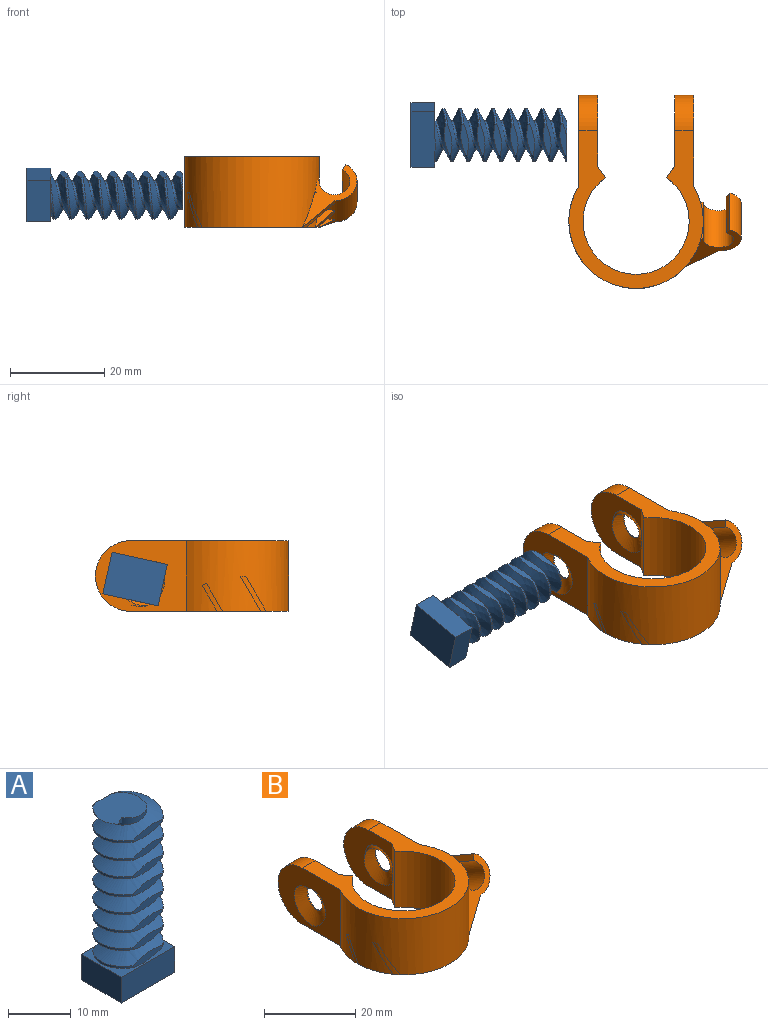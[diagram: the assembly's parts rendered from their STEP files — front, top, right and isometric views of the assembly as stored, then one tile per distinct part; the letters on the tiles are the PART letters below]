
ASSEMBLY  parts=2 mates=1
PART A: 45 faces, bbox 13.5x14.4x36.2 mm
  f0: bspline ~30.47x12.93mm, area 544.1mm2, adj f2,f3,f4,f5,f6,f7,f8,f9
  f1: bspline ~4.85x4.1mm, area 0.1mm2, adj f20,f22,f29
  f2: cylinder r=5.6mm len=9mm, axis (0,0,1), area 4.2mm2, adj f0,f18,f29,f37
  f3: cylinder r=5.6mm len=9mm, axis (0,0,1), area 4.2mm2, adj f0,f18,f30,f38
  f4: cylinder r=5.6mm len=9mm, axis (0,0,1), area 4.2mm2, adj f0,f18,f31,f39
  f5: cylinder r=5.6mm len=9mm, axis (0,0,1), area 4.2mm2, adj f0,f18,f32,f40
  f6: cylinder r=5.6mm len=9mm, axis (0,0,1), area 4.2mm2, adj f0,f18,f33,f41
  f7: cylinder r=5.6mm len=9mm, axis (0,0,1), area 4.2mm2, adj f0,f18,f34,f42
  f8: cylinder r=5.6mm len=9mm, axis (0,0,1), area 4.2mm2, adj f0,f18,f35,f43
  f9: cylinder r=5.6mm len=9mm, axis (0,0,1), area 4.2mm2, adj f0,f18,f36,f44
  f10: cylinder r=5.6mm len=8.51mm, axis (0,0,1), area 3.1mm2, adj f0,f18,f23,f44
  f11: cylinder r=5.6mm len=9mm, axis (0,0,1), area 4.2mm2, adj f0,f18,f36,f43
  f12: cylinder r=5.6mm len=9mm, axis (0,0,1), area 4.2mm2, adj f0,f18,f35,f42
  f13: cylinder r=5.6mm len=9mm, axis (0,0,1), area 4.2mm2, adj f0,f18,f34,f41
  f14: cylinder r=5.6mm len=9mm, axis (0,0,1), area 4.2mm2, adj f0,f18,f33,f40
  f15: cylinder r=5.6mm len=9mm, axis (0,0,1), area 4.2mm2, adj f0,f18,f32,f39
  f16: cylinder r=5.6mm len=9mm, axis (0,0,1), area 4.2mm2, adj f0,f18,f31,f38
  f17: cylinder r=5.6mm len=9mm, axis (0,0,1), area 4.2mm2, adj f0,f18,f30,f37
  f18: bspline ~30.47x12.93mm, area 534.8mm2, adj f2,f3,f4,f5,f6,f7,f8,f9
  f19: plane 1.81x1mm, normal (0.43,-0.9,0), area 1mm2, adj f18,f21,f22
  f20: cylinder r=5.6mm len=3.96mm, axis (0,0,1), area 1.1mm2, adj f1,f18,f22,f29
  f21: cylinder r=3mm len=28mm, axis (0,0,-1), area 44.6mm2, adj f0,f18,f19,f22,f23
  f22: plane 9.26x8.01mm, normal (0,0,1), area 52.2mm2, adj f0,f1,f18,f19,f20,f21,f29
  f23: plane 13.5x10.5mm, normal (0,0,1), area 49.2mm2, adj f0,f10,f18,f21,f24,f25,f26,f27
  f24: plane 9x5mm, normal (1,0,0), area 45mm2, adj f23,f25,f27,f28
  f25: plane 12.82x6.02mm, normal (0,1,0), area 60.5mm2, adj f0,f23,f24,f26,f28
  f26: plane 9x5mm, normal (-1,0,0), area 45mm2, adj f23,f25,f27,f28
  f27: plane 12x5mm, normal (0,-1,0), area 60mm2, adj f23,f24,f26,f28
  f28: plane 12x9mm, normal (0,0,-1), area 108mm2, adj f24,f25,f26,f27
  f29: plane 7.04x1.82mm, normal (0,1,0), area 7mm2, adj f0,f1,f2,f18,f20,f22
  f30: plane 6.67x1.65mm, normal (0,1,0), area 7.4mm2, adj f0,f3,f17,f18
  f31: plane 6.67x1.65mm, normal (0,1,0), area 7.4mm2, adj f0,f4,f16,f18
  f32: plane 6.67x1.65mm, normal (0,1,0), area 7.4mm2, adj f0,f5,f15,f18
  f33: plane 6.67x1.65mm, normal (0,1,0), area 7.4mm2, adj f0,f6,f14,f18
  f34: plane 6.67x1.65mm, normal (0,1,0), area 7.4mm2, adj f0,f7,f13,f18
  f35: plane 6.67x1.65mm, normal (0,1,0), area 7.4mm2, adj f0,f8,f12,f18
  f36: plane 6.67x1.65mm, normal (0,1,0), area 7.4mm2, adj f0,f9,f11,f18
  f37: plane 6.67x1.65mm, normal (0,-1,0), area 7.4mm2, adj f0,f2,f17,f18
  f38: plane 6.67x1.65mm, normal (0,-1,0), area 7.4mm2, adj f0,f3,f16,f18
  f39: plane 6.67x1.65mm, normal (0,-1,0), area 7.4mm2, adj f0,f4,f15,f18
  f40: plane 6.67x1.65mm, normal (0,-1,0), area 7.4mm2, adj f0,f5,f14,f18
  f41: plane 6.67x1.65mm, normal (0,-1,0), area 7.4mm2, adj f0,f6,f13,f18
  f42: plane 6.67x1.65mm, normal (0,-1,0), area 7.4mm2, adj f0,f7,f12,f18
  f43: plane 6.67x1.65mm, normal (0,-1,0), area 7.4mm2, adj f0,f8,f11,f18
  f44: plane 6.67x1.65mm, normal (0,-1,0), area 7.4mm2, adj f0,f9,f10,f18
PART B: 37 faces, bbox 38.5x42.8x16.9 mm
  f0: cylinder r=3.15mm len=6.3mm, axis (-1,0,0), area 4.5mm2, adj f13,f14,f31,f32
  f1: cylinder r=3.15mm len=6.3mm, axis (-1,0,0), area 4.5mm2, adj f8,f9,f33,f34
  f2: cylinder r=4.75mm len=0.48mm, axis (0,-0.87,0.5), area 0.1mm2, adj f3,f22,f23
  f3: cylinder r=14.25mm len=28.5mm, axis (0,0,1), area 804.6mm2, adj f2,f4,f6,f8,f14,f15,f16,f20
  f4: cylinder r=14.25mm len=7.5mm, axis (0,0,1), area 10.2mm2, adj f3,f15
  f5: cylinder r=14.25mm len=5.07mm, axis (0,0,1), area 12.3mm2, adj f15,f19,f27,f30
  f6: cylinder r=14.25mm len=6mm, axis (0,0,1), area 6.7mm2, adj f3,f15
  f7: cylinder r=14.25mm len=6.94mm, axis (0,0,1), area 22.4mm2, adj f15,f19,f25,f28
  f8: plane 19.27x15mm, normal (1,0,0), area 192.2mm2, adj f1,f3,f15,f16,f33,f34,f36
  f9: plane 16.91x16.91mm, normal (-1,0,0), area 131.3mm2, adj f1,f10,f15,f16,f33,f34,f36
  f10: plane 15.88x3.33mm, normal (-0.82,0.57,0), area 42.1mm2, adj f9,f11,f15,f16,f33,f34
  f11: cylinder r=11.25mm len=22.5mm, axis (0,0,1), area 854.1mm2, adj f10,f12,f15,f16
  f12: plane 15x2.46mm, normal (0.82,0.57,0), area 45mm2, adj f11,f13,f15,f16
  f13: plane 15x15mm, normal (1,0,0), area 128.1mm2, adj f0,f12,f15,f16,f31,f32,f35
  f14: plane 19.27x15mm, normal (-1,0,0), area 192.1mm2, adj f0,f3,f15,f16,f31,f32,f35
  f15: plane 33.42x28.5mm, normal (0,0,-1), area 268.3mm2, adj f3,f4,f5,f6,f7,f8,f9,f10
  f16: plane 33.42x28.5mm, normal (0,0,1), area 268.3mm2, adj f3,f8,f9,f10,f11,f12,f13,f14
  f17: cylinder r=3.25mm len=10.83mm, axis (0,-0.87,0.5), area 125.1mm2, adj f18,f20,f21,f22
  f18: plane 8.44x5.63mm, normal (-0.87,0.25,0.43), area 13.5mm2, adj f17,f19,f21,f22
  f19: cylinder r=4.75mm len=12.23mm, axis (0,-0.87,0.5), area 135.4mm2, adj f5,f7,f18,f21,f22,f24,f25,f26
  f20: plane 7.94x4.66mm, normal (0.09,0.5,0.86), area 1.7mm2, adj f3,f17,f21,f22
  f21: plane 8.87x8.65mm, normal (0,0.87,-0.5), area 26.5mm2, adj f3,f17,f18,f19,f20,f29
  f22: plane 13.33x11.67mm, normal (0,-0.87,0.5), area 42.1mm2, adj f2,f3,f17,f18,f19,f20,f23,f24
  f23: bspline ~4.23x1.06mm, area 0.1mm2, adj f2,f3,f22
  f24: bspline ~6.9x5.64mm, area 9mm2, adj f15,f19,f22,f25
  f25: plane 7.22x6.25mm, normal (0,0.87,-0.5), area 15.2mm2, adj f7,f19,f24
  f26: bspline ~4.12x3.63mm, area 5.6mm2, adj f15,f19,f27,f28
  f27: plane 4.33x3.78mm, normal (0,0.87,-0.5), area 7.5mm2, adj f5,f19,f26
  f28: plane 4.94x4.18mm, normal (0,-0.87,0.5), area 8.9mm2, adj f7,f19,f26
  f29: bspline ~3.28x1.81mm, area 3.8mm2, adj f15,f19,f21,f30
  f30: plane 3.32x2.8mm, normal (0,-0.87,0.5), area 4.4mm2, adj f5,f19,f29
  f31: bspline ~14.9x12.9mm, area 127.9mm2, adj f0,f13,f14,f32
  f32: bspline ~14.9x12.9mm, area 127.9mm2, adj f0,f13,f14,f31
  f33: bspline ~14.9x12.9mm, area 129.4mm2, adj f1,f8,f9,f10,f34
  f34: bspline ~14.9x12.9mm, area 128.6mm2, adj f1,f8,f9,f10,f33
  f35: cylinder r=7.5mm len=15mm, axis (1,0,0), area 94.2mm2, adj f13,f14,f15,f16
  f36: cylinder r=7.5mm len=15mm, axis (1,0,0), area 94.2mm2, adj f8,f9,f15,f16
PLACE A rot(axis=(0.61,0.49,0.61),127.4deg) t=(-42.71,18.27,6.84)mm
PLACE B t=(0,0,7.5)mm
MATE cylindrical A.f22 <-> B.f0  axis (1,0,0) through (-14.71,17.04,7.5)mm
